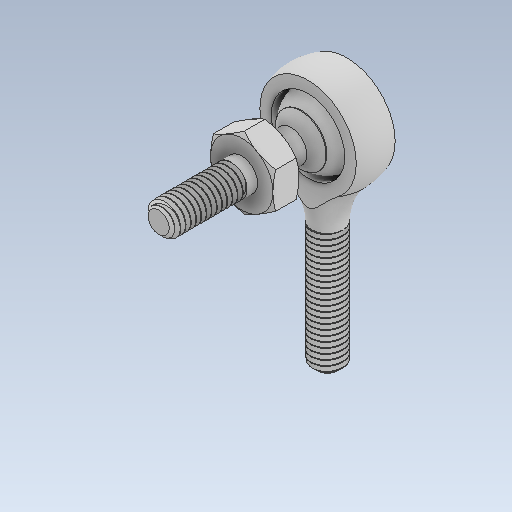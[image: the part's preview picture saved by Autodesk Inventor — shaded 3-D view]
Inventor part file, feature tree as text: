
AUTODESK INVENTOR PART (.ipt)
format: ipt  version: 2023 (Build 270158000, 158)  size: 859,136 bytes
history: native  units: in
note: dims shown in document units (in); Inventor stores cm internally (conversion verified against a paired STEP export)
features: other x1, chamfer x1, revolve x1
ambient origin geometry x8: Origin, YZ Plane, XZ Plane, XY Plane, X Axis, Y Axis, Z Axis, Center Point
bodies: Solid1 (feature_tree), Solid2 (feature_tree), Solid3 (feature_tree)
feature tree (3):
  other  "Cut-Extrude2"
  chamfer  "Chamfer1"  [1 undecoded]
  revolve  "Revolve6"  [1 undecoded]
note: 2 required parameter values undecoded (feature->parameter linkage not recoverable at this tier; creation-order binding heuristic only, values carry confidence <= 0.55)
